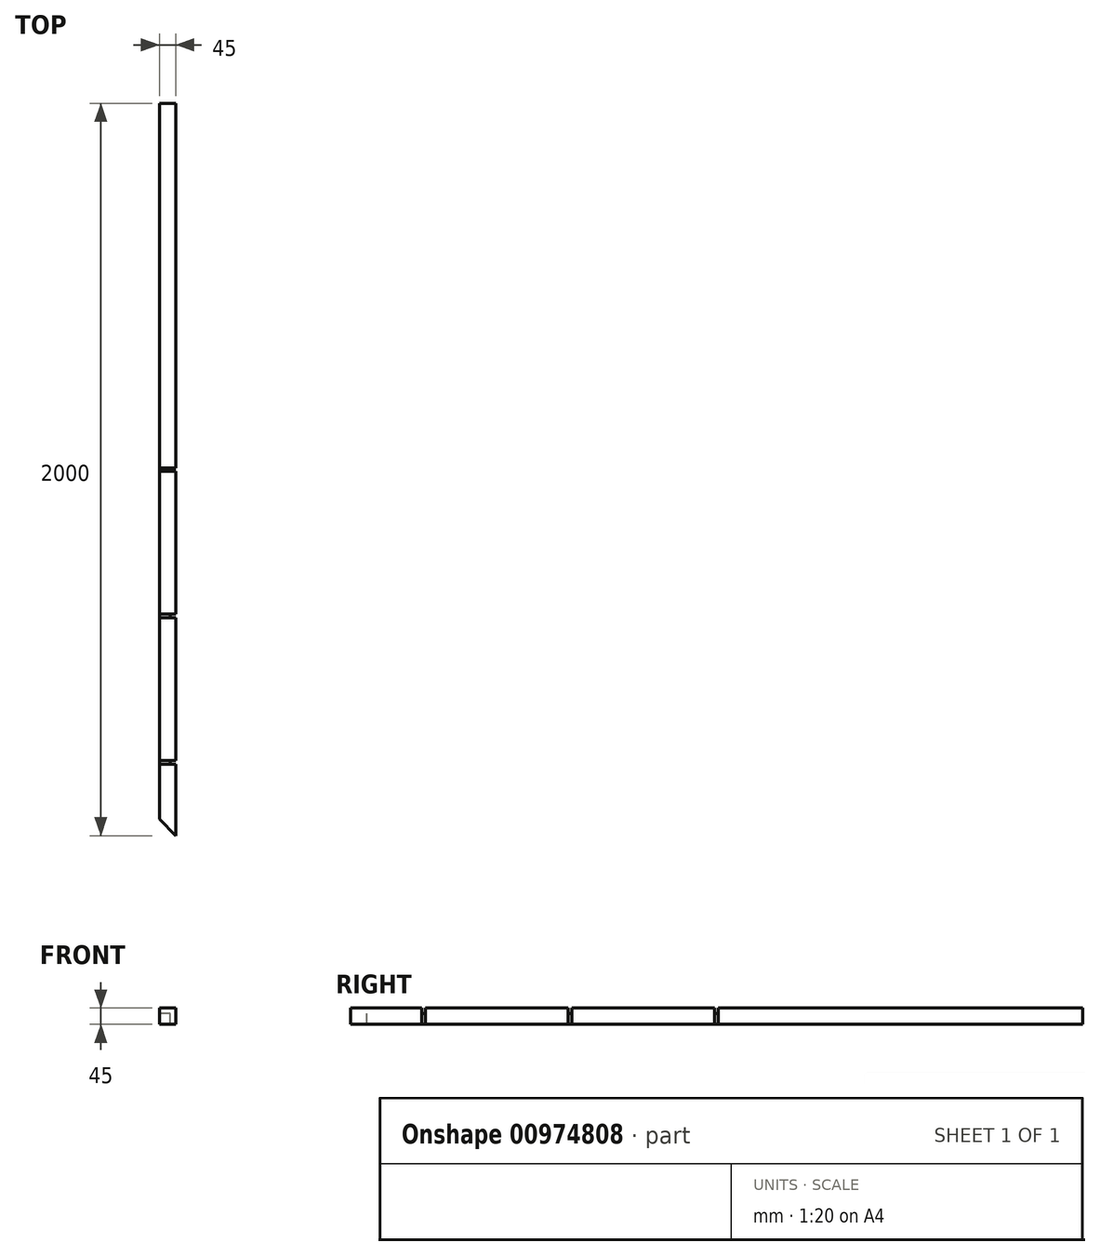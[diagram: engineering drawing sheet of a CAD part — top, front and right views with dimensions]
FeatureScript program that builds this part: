
annotation { "Feature Type Name" : "Feature", "Feature Type Description" : "" }
export const myFeature = defineFeature(function(context is Context, id is Id, definition is map)
    precondition{}
    {
        {
            var Q0;
            Q0=qCreatedBy(makeId("Front.planeOp"),FACE);
            var sketch = newSketch(context, id + "F0", { "sketchPlane" : qUnion([Q0])});
            skLineSegment(sketch, "E0.bottom", {"start": v(22.5, -22.5) * mm, "end": v(-22.5, -22.5) * mm});
            skLineSegment(sketch, "E0.top", {"start": v(22.5, 22.5) * mm, "end": v(-22.5, 22.5) * mm});
            skLineSegment(sketch, "E0.left", {"start": v(22.5, -22.5) * mm, "end": v(22.5, 22.5) * mm});
            skLineSegment(sketch, "E0.right", {"start": v(-22.5, -22.5) * mm, "end": v(-22.5, 22.5) * mm});
            skPoint(sketch, "E0.middle", {"position": v(0, 0) * mm});
            skSolve(sketch);
        }
        {
            var Q0;
            Q0 = qSketchRegion(id + "F0", true);
            extrude(context, id + "F1", {"entities" : qUnion([Q0]), "endBound" : BoundingType.SYMMETRIC, "depth" : 3000 * mm, "offsetDistance" : 25 * mm});
        }
        {
            var Q0;
            Q0=makeQuery(id+"F1.opExtrude","SWEPT_FACE",FACE,{"disambiguationData":[OSD([sQuery(id+"F0.wireOp",EDGE,"E0.top")])]});
            var sketch = newSketch(context, id + "F2", { "sketchPlane" : qUnion([Q0])});
            skLineSegment(sketch, "E1", {"start": v(-22.5, -955) * mm, "end": v(22.5, -1000) * mm});
            skLineSegment(sketch, "E2", {"start": v(22.5, -1000) * mm, "end": v(22.5, -1500) * mm});
            skLineSegment(sketch, "E3", {"start": v(22.5, -1500) * mm, "end": v(-22.5, -1500) * mm});
            skLineSegment(sketch, "E4", {"start": v(-22.5, -1500) * mm, "end": v(-22.5, -955) * mm});
            skLineSegment(sketch, "E5", {"start": v(22.5, 1500) * mm, "end": v(22.5, 1000) * mm});
            skLineSegment(sketch, "E6", {"start": v(22.5, 1000) * mm, "end": v(-22.5, 1000) * mm});
            skLineSegment(sketch, "E7", {"start": v(-22.5, 1000) * mm, "end": v(-22.5, 1500) * mm});
            skLineSegment(sketch, "E8", {"start": v(-22.5, 1500) * mm, "end": v(22.5, 1500) * mm});
            skSolve(sketch);
        }
        {
            var Q0;
            Q0 = qSketchRegion(id + "F2", true);
            extrude(context, id + "F3", {"entities" : qUnion([Q0]), "operationType" : NewBodyOperationType.REMOVE, "endBound" : BoundingType.UP_TO_NEXT, "oppositeDirection" : true, "depth" : 25 * mm, "offsetDistance" : 25 * mm});
        }
        {
            var Q0;
            Q0=qCreatedBy(makeId("Front.planeOp"),FACE);
            var sketch = newSketch(context, id + "F4", { "sketchPlane" : qUnion([Q0])});
            skLineSegment(sketch, "E9", {"start": v(-22.5, 22.5) * mm, "end": v(22.5, 22.5) * mm});
            skLineSegment(sketch, "E10", {"start": v(22.5, 22.5) * mm, "end": v(22.5, -22.5) * mm});
            skLineSegment(sketch, "E11", {"start": v(22.5, -22.5) * mm, "end": v(7.5, -22.5) * mm});
            skLineSegment(sketch, "E12", {"start": v(7.5, -22.5) * mm, "end": v(7.5, 7.5) * mm});
            skLineSegment(sketch, "E13", {"start": v(7.5, 7.5) * mm, "end": v(-22.5, 7.5) * mm});
            skLineSegment(sketch, "E14", {"start": v(-22.5, 7.5) * mm, "end": v(-22.5, 22.5) * mm});
            skSolve(sketch);
        }
        {
            var Q0;
            Q0 = qSketchRegion(id + "F4", true);
            extrude(context, id + "F5", {"entities" : qUnion([Q0]), "operationType" : NewBodyOperationType.REMOVE, "endBound" : BoundingType.SYMMETRIC, "oppositeDirection" : true, "depth" : 10 * mm, "offsetDistance" : 25 * mm});
        }
        {
            var Q0;
            Q0=qCreatedBy(makeId("Front.planeOp"),FACE);
            cPlane(context, id + "F6", {"entities" : qUnion([Q0]), "cplaneType" : CPlaneType.OFFSET, "offset" : 400 * mm, "width" : 150 * mm, "height" : 150 * mm});
        }
        {
            var Q0;
            Q0=qCreatedBy(id+"F6.planeOp",FACE);
            var sketch = newSketch(context, id + "F7", { "sketchPlane" : qUnion([Q0])});
            skLineSegment(sketch, "E15.0", {"start": v(-22.5, 7.5) * mm, "end": v(-22.5, 22.5) * mm});
            skLineSegment(sketch, "E16.0", {"start": v(-22.5, 22.5) * mm, "end": v(22.5, 22.5) * mm});
            skLineSegment(sketch, "E17.0", {"start": v(7.5, 7.5) * mm, "end": v(-22.5, 7.5) * mm});
            skLineSegment(sketch, "E18.0", {"start": v(7.5, -22.5) * mm, "end": v(7.5, 7.5) * mm});
            skLineSegment(sketch, "E19.0", {"start": v(22.5, -22.5) * mm, "end": v(7.5, -22.5) * mm});
            skLineSegment(sketch, "E20.0", {"start": v(22.5, 22.5) * mm, "end": v(22.5, -22.5) * mm});
            skSolve(sketch);
        }
        {
            var Q0;
            Q0 = qSketchRegion(id + "F7", true);
            extrude(context, id + "F8", {"entities" : qUnion([Q0]), "operationType" : NewBodyOperationType.REMOVE, "endBound" : BoundingType.SYMMETRIC, "oppositeDirection" : true, "depth" : 10 * mm, "offsetDistance" : 25 * mm});
        }
        {
            var Q0;
            Q0=qCreatedBy(makeId("Front.planeOp"),FACE);
            cPlane(context, id + "F9", {"entities" : qUnion([Q0]), "cplaneType" : CPlaneType.OFFSET, "offset" : 800 * mm, "width" : 150 * mm, "height" : 150 * mm});
        }
        {
            var Q0;
            Q0=qCreatedBy(id+"F9.planeOp",FACE);
            var sketch = newSketch(context, id + "F10", { "sketchPlane" : qUnion([Q0])});
            skLineSegment(sketch, "E21.0", {"start": v(-22.5, 7.5) * mm, "end": v(-22.5, 22.5) * mm});
            skLineSegment(sketch, "E22.0", {"start": v(-22.5, 22.5) * mm, "end": v(22.5, 22.5) * mm});
            skLineSegment(sketch, "E23.0", {"start": v(22.5, 22.5) * mm, "end": v(22.5, -22.5) * mm});
            skLineSegment(sketch, "E24.0", {"start": v(22.5, -22.5) * mm, "end": v(7.5, -22.5) * mm});
            skLineSegment(sketch, "E25.0", {"start": v(7.5, -22.5) * mm, "end": v(7.5, 7.5) * mm});
            skLineSegment(sketch, "E26.0", {"start": v(7.5, 7.5) * mm, "end": v(-22.5, 7.5) * mm});
            skSolve(sketch);
        }
        {
            var Q0;
            Q0 = qSketchRegion(id + "F10", true);
            extrude(context, id + "F11", {"entities" : qUnion([Q0]), "operationType" : NewBodyOperationType.REMOVE, "endBound" : BoundingType.SYMMETRIC, "oppositeDirection" : true, "depth" : 10 * mm, "offsetDistance" : 25 * mm});
        }
    });
